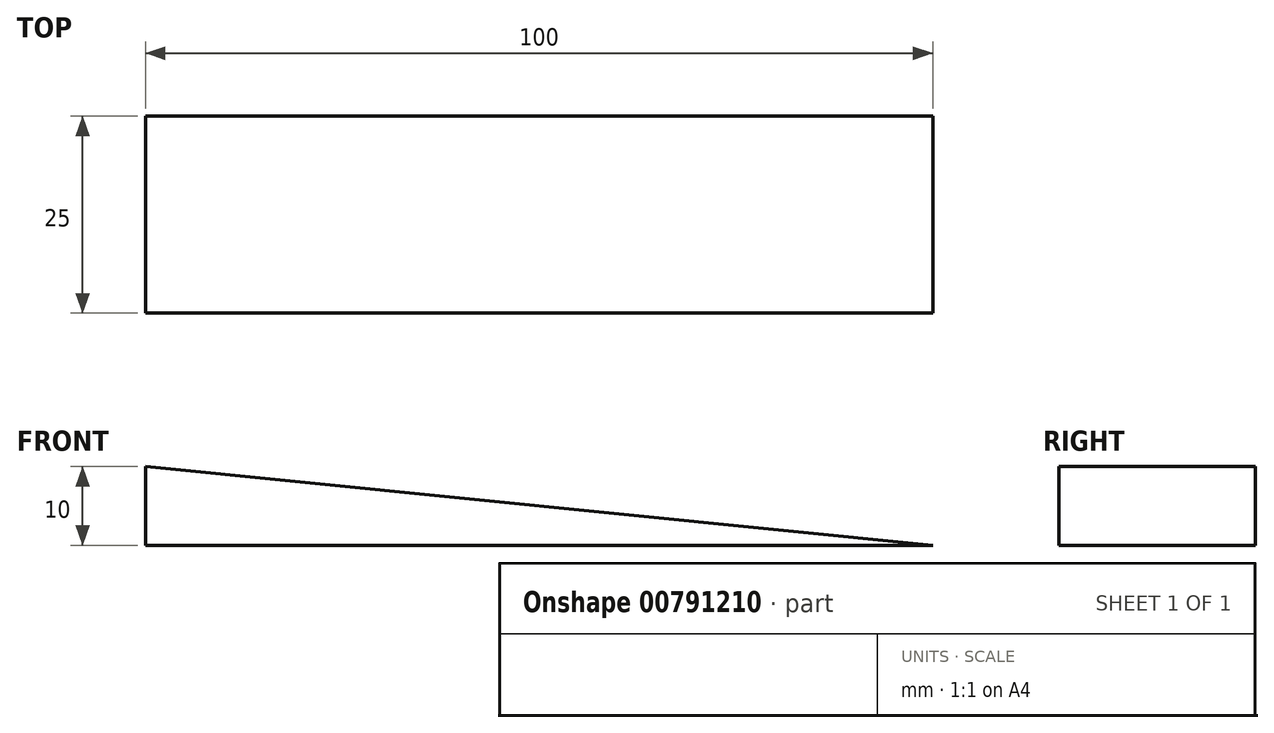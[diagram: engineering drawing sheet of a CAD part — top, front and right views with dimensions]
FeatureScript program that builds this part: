
annotation { "Feature Type Name" : "Feature", "Feature Type Description" : "" }
export const myFeature = defineFeature(function(context is Context, id is Id, definition is map)
    precondition{}
    {
        {
            var Q0;
            Q0=qCreatedBy(makeId("Front.planeOp"),FACE);
            var sketch = newSketch(context, id + "F0", { "sketchPlane" : qUnion([Q0])});
            skLineSegment(sketch, "E0", {"start": v(-21.38, 2.17) * mm, "end": v(-21.38, -7.83) * mm});
            skLineSegment(sketch, "E1", {"start": v(-21.38, -7.83) * mm, "end": v(78.62, -7.83) * mm});
            skLineSegment(sketch, "E2", {"start": v(78.62, -7.83) * mm, "end": v(-21.38, 2.17) * mm});
            skSolve(sketch);
        }
        {
            var Q0;
            Q0=makeQuery(id+"F0.imprint","IMPRINT",FACE,{"disambiguationData":[TD([[makeQuery(id+"F0.imprint","IMPRINT",EDGE,{"derivedFrom":sQuery(id+"F0.wireOp",EDGE,"E0")}),1.0]])]});
            extrude(context, id + "F1", {"entities" : qUnion([Q0]), "depth" : 25 * mm, "offsetDistance" : 25 * mm});
        }
    });
